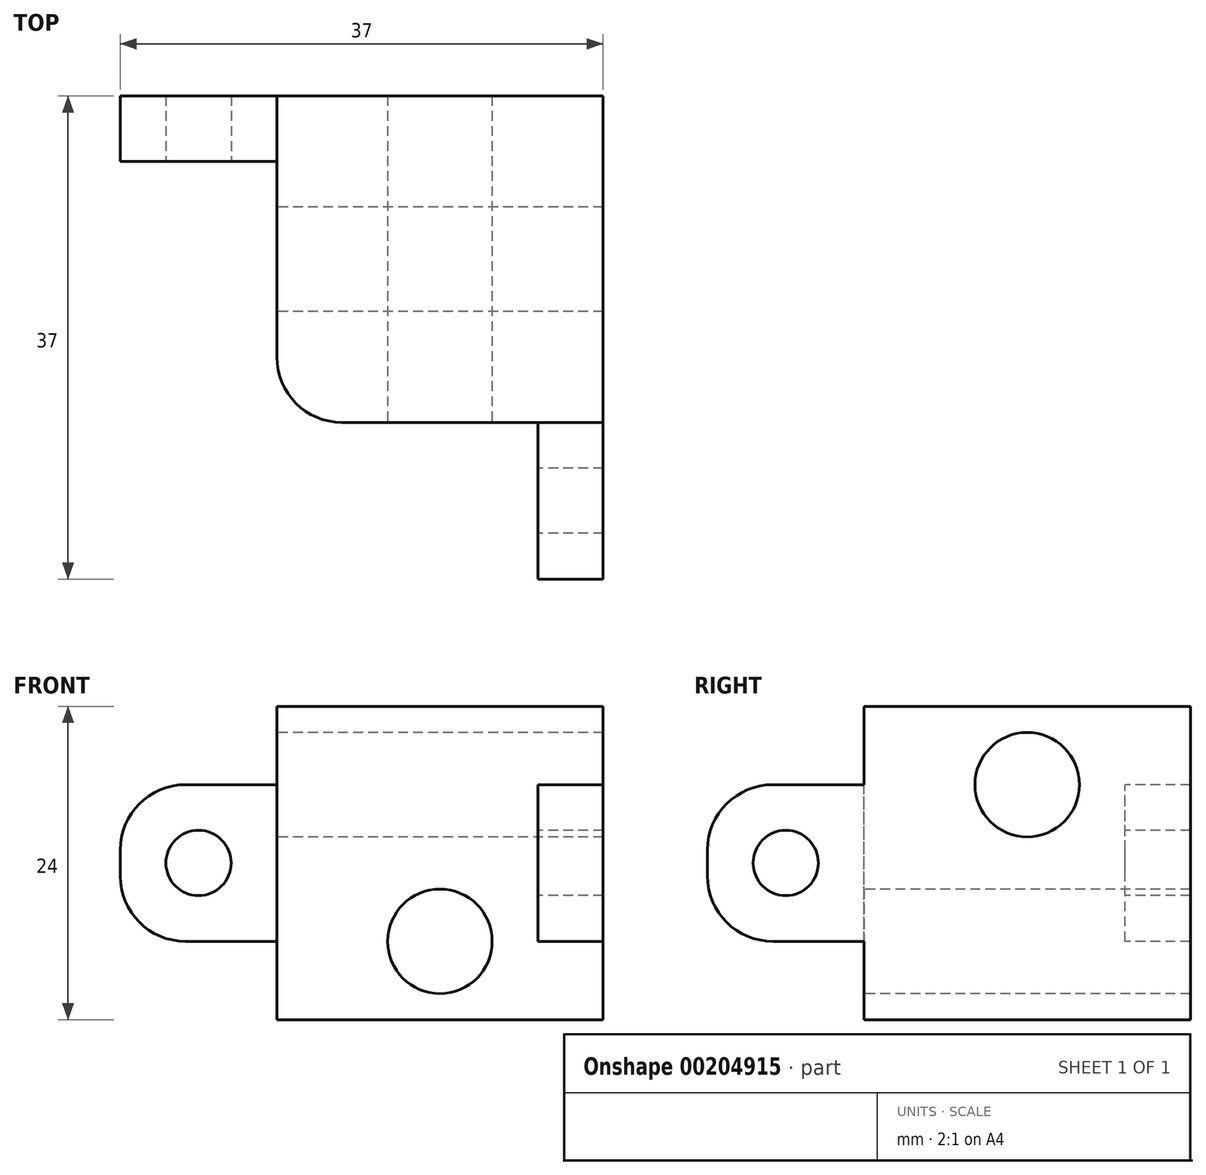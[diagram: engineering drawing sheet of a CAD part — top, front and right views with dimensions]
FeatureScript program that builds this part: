
annotation { "Feature Type Name" : "Feature", "Feature Type Description" : "" }
export const myFeature = defineFeature(function(context is Context, id is Id, definition is map)
    precondition{}
    {
        {
            var Q0;
            Q0=qCreatedBy(makeId("Front.planeOp"),FACE);
            var sketch = newSketch(context, id + "F0", { "sketchPlane" : qUnion([Q0])});
            skLineSegment(sketch, "E0.bottom", {"start": v(0, 0) * mm, "end": v(25, 0) * mm});
            skLineSegment(sketch, "E0.top", {"start": v(0, 45) * mm, "end": v(25, 45) * mm});
            skLineSegment(sketch, "E0.left", {"start": v(0, 0) * mm, "end": v(0, 45) * mm});
            skLineSegment(sketch, "E0.right", {"start": v(25, 0) * mm, "end": v(25, 45) * mm});
            skSolve(sketch);
        }
        {
            var Q0;
            Q0=makeQuery(id+"F0.imprint","IMPRINT",FACE,{"disambiguationData":[TD([[makeQuery(id+"F0.imprint","IMPRINT",EDGE,{"derivedFrom":sQuery(id+"F0.wireOp",EDGE,"E0.bottom")}),1.0]])]});
            extrude(context, id + "F1", {"entities" : qUnion([Q0]), "depth" : 25 * mm});
        }
        {
            var Q0;
            Q0=makeQuery(id+"F1.opExtrude","CAP_FACE",FACE,{"disambiguationData":[OSD([sQuery(id+"F0.wireOp",EDGE,"E0.bottom"),sQuery(id+"F0.wireOp",EDGE,"E0.top"),sQuery(id+"F0.wireOp",EDGE,"E0.left"),sQuery(id+"F0.wireOp",EDGE,"E0.right")])],"isStart":false});
            var sketch = newSketch(context, id + "F2", { "sketchPlane" : qUnion([Q0])});
            skLineSegment(sketch, "E1", {"start": v(12.5, 0) * mm, "end": v(12.5, 25) * mm});
            skCircle(sketch, "E2", {"center": v(12.5, 25) * mm, "radius": 4 * mm});
            skSolve(sketch);
        }
        {
            var Q0;
            Q0=makeQuery(id+"F2.imprint","IMPRINT",FACE,{"disambiguationData":[TD([[makeQuery(id+"F2.imprint","IMPRINT",EDGE,{"derivedFrom":sQuery(id+"F2.wireOp",EDGE,"E2")}),1.0]])]});
            extrude(context, id + "F3", {"entities" : qUnion([Q0]), "operationType" : NewBodyOperationType.REMOVE, "oppositeDirection" : true, "depth" : 25 * mm});
        }
        {
            var Q0;
            Q0=makeQuery(id+"F1.opExtrude","SWEPT_FACE",FACE,{"disambiguationData":[OSD([sQuery(id+"F0.wireOp",EDGE,"E0.left")])]});
            var sketch = newSketch(context, id + "F4", { "sketchPlane" : qUnion([Q0])});
            skLineSegment(sketch, "E3", {"start": v(12.5, 0) * mm, "end": v(12.5, 37) * mm});
            skCircle(sketch, "E4", {"center": v(12.5, 37) * mm, "radius": 4 * mm});
            skSolve(sketch);
        }
        {
            var Q0;
            Q0=makeQuery(id+"F4.imprint","IMPRINT",FACE,{"disambiguationData":[TD([[makeQuery(id+"F4.imprint","IMPRINT",EDGE,{"derivedFrom":sQuery(id+"F4.wireOp",EDGE,"E4")}),1.0]])]});
            extrude(context, id + "F5", {"entities" : qUnion([Q0]), "operationType" : NewBodyOperationType.REMOVE, "oppositeDirection" : true, "depth" : 25 * mm});
        }
        {
            var Q0;
            Q0=makeQuery(id+"F1.opExtrude","SWEPT_FACE",FACE,{"disambiguationData":[OSD([sQuery(id+"F0.wireOp",EDGE,"E0.left")])]});
            var sketch = newSketch(context, id + "F6", { "sketchPlane" : qUnion([Q0])});
            skLineSegment(sketch, "E5.bottom", {"start": v(0, 25) * mm, "end": v(5, 25) * mm});
            skLineSegment(sketch, "E5.top", {"start": v(0, 37) * mm, "end": v(5, 37) * mm});
            skLineSegment(sketch, "E5.left", {"start": v(0, 25) * mm, "end": v(0, 37) * mm});
            skLineSegment(sketch, "E5.right", {"start": v(5, 25) * mm, "end": v(5, 37) * mm});
            skSolve(sketch);
        }
        {
            var Q0;
            Q0=makeQuery(id+"F6.imprint","IMPRINT",FACE,{"disambiguationData":[TD([[makeQuery(id+"F6.imprint","IMPRINT",EDGE,{"derivedFrom":sQuery(id+"F6.wireOp",EDGE,"E5.bottom")}),1.0]])]});
            extrude(context, id + "F7", {"entities" : qUnion([Q0]), "operationType" : NewBodyOperationType.ADD, "depth" : 12 * mm});
        }
        {
            var Q0;
            Q0=makeQuery(id+"F7.opExtrude","SWEPT_FACE",FACE,{"disambiguationData":[OSD([sQuery(id+"F6.wireOp",EDGE,"E5.right")])]});
            var sketch = newSketch(context, id + "F8", { "sketchPlane" : qUnion([Q0])});
            skLineSegment(sketch, "E6", {"start": v(-6, 25) * mm, "end": v(-6, 37) * mm});
            skCircle(sketch, "E7", {"center": v(-6, 31) * mm, "radius": 2.5 * mm});
            skSolve(sketch);
        }
        {
            var Q0;
            {var subQ0=sQuery(id+"F8.wireOp",EDGE,"E7");var subQ1=sQuery(id+"F8.wireOp",EDGE,"E6");var subQ2=makeQuery(id+"F8.imprint","INTERSECT",VERTEX,{"disambiguationData":[OD(0.0)],"derivedFrom":[subQ1,subQ0]});Q0=makeQuery(id+"F8.imprint","IMPRINT",FACE,{"disambiguationData":[TD([[makeQuery(id+"F8.imprint","IMPRINT",EDGE,{"disambiguationData":[TD([[subQ2,-1.0]])],"derivedFrom":subQ1}),1.0]])]});}
            var Q1;
            {var subQ0=sQuery(id+"F8.wireOp",EDGE,"E7");var subQ1=sQuery(id+"F8.wireOp",EDGE,"E6");var subQ2=makeQuery(id+"F8.imprint","INTERSECT",VERTEX,{"disambiguationData":[OD(0.0)],"derivedFrom":[subQ1,subQ0]});Q1=makeQuery(id+"F8.imprint","IMPRINT",FACE,{"disambiguationData":[TD([[makeQuery(id+"F8.imprint","IMPRINT",EDGE,{"disambiguationData":[TD([[subQ2,-1.0]])],"derivedFrom":subQ1}),-1.0]])]});}
            extrude(context, id + "F9", {"entities" : qUnion([Q0, Q1]), "operationType" : NewBodyOperationType.REMOVE, "oppositeDirection" : true, "depth" : 25 * mm});
        }
        {
            var Q0;
            Q0=makeQuery(id+"F7.opExtrude","CAP_EDGE",EDGE,{"disambiguationData":[OSD([sQuery(id+"F6.wireOp",EDGE,"E5.top")])],"isStart":false});
            var Q1;
            Q1=makeQuery(id+"F7.opExtrude","CAP_EDGE",EDGE,{"disambiguationData":[OSD([sQuery(id+"F6.wireOp",EDGE,"E5.bottom")])],"isStart":false});
            var Q2;
            Q2=makeQuery(id+"F7.opExtrude","CAP_EDGE",EDGE,{"disambiguationData":[OSD([sQuery(id+"F6.wireOp",EDGE,"E5.top")])],"isStart":true});
            fillet(context, id + "F10", {"entities" : qUnion([Q0, Q1, Q2]), "radius" : 5 * mm, "tangentPropagation" : true, "allowEdgeOverflow" : false});
        }
        {
            var Q0;
            Q0=makeQuery(id+"F1.opExtrude","CAP_FACE",FACE,{"disambiguationData":[OSD([sQuery(id+"F0.wireOp",EDGE,"E0.bottom"),sQuery(id+"F0.wireOp",EDGE,"E0.top"),sQuery(id+"F0.wireOp",EDGE,"E0.left"),sQuery(id+"F0.wireOp",EDGE,"E0.right")])],"isStart":false});
            var sketch = newSketch(context, id + "F11", { "sketchPlane" : qUnion([Q0])});
            skLineSegment(sketch, "E8.bottom", {"start": v(25, 25) * mm, "end": v(20, 25) * mm});
            skLineSegment(sketch, "E8.top", {"start": v(25, 37) * mm, "end": v(20, 37) * mm});
            skLineSegment(sketch, "E8.left", {"start": v(25, 25) * mm, "end": v(25, 37) * mm});
            skLineSegment(sketch, "E8.right", {"start": v(20, 25) * mm, "end": v(20, 37) * mm});
            skSolve(sketch);
        }
        {
            var Q0;
            Q0=makeQuery(id+"F11.imprint","IMPRINT",FACE,{"disambiguationData":[TD([[makeQuery(id+"F11.imprint","IMPRINT",EDGE,{"derivedFrom":sQuery(id+"F11.wireOp",EDGE,"E8.bottom")}),-1.0]])]});
            extrude(context, id + "F12", {"entities" : qUnion([Q0]), "operationType" : NewBodyOperationType.ADD, "depth" : 12 * mm});
        }
        {
            var Q0;
            Q0=makeQuery(id+"F12.opExtrude","SWEPT_FACE",FACE,{"disambiguationData":[OSD([sQuery(id+"F11.wireOp",EDGE,"E8.right")])]});
            var sketch = newSketch(context, id + "F13", { "sketchPlane" : qUnion([Q0])});
            skLineSegment(sketch, "E9", {"start": v(31, 25) * mm, "end": v(31, 37) * mm});
            skCircle(sketch, "E10", {"center": v(31, 31) * mm, "radius": 2.5 * mm});
            skSolve(sketch);
        }
        {
            var Q0;
            {var subQ0=sQuery(id+"F13.wireOp",EDGE,"E10");var subQ1=sQuery(id+"F13.wireOp",EDGE,"E9");var subQ2=makeQuery(id+"F13.imprint","INTERSECT",VERTEX,{"disambiguationData":[OD(0.0)],"derivedFrom":[subQ1,subQ0]});Q0=makeQuery(id+"F13.imprint","IMPRINT",FACE,{"disambiguationData":[TD([[makeQuery(id+"F13.imprint","IMPRINT",EDGE,{"disambiguationData":[TD([[subQ2,-1.0]])],"derivedFrom":subQ1}),1.0]])]});}
            var Q1;
            {var subQ0=sQuery(id+"F13.wireOp",EDGE,"E10");var subQ1=sQuery(id+"F13.wireOp",EDGE,"E9");var subQ2=makeQuery(id+"F13.imprint","INTERSECT",VERTEX,{"disambiguationData":[OD(0.0)],"derivedFrom":[subQ1,subQ0]});Q1=makeQuery(id+"F13.imprint","IMPRINT",FACE,{"disambiguationData":[TD([[makeQuery(id+"F13.imprint","IMPRINT",EDGE,{"disambiguationData":[TD([[subQ2,-1.0]])],"derivedFrom":subQ1}),-1.0]])]});}
            extrude(context, id + "F14", {"entities" : qUnion([Q0, Q1]), "operationType" : NewBodyOperationType.REMOVE, "oppositeDirection" : true, "depth" : 25 * mm});
        }
        {
            var Q0;
            Q0=makeQuery(id+"F12.opExtrude","CAP_EDGE",EDGE,{"disambiguationData":[OSD([sQuery(id+"F11.wireOp",EDGE,"E8.top")])],"isStart":false});
            var Q1;
            Q1=makeQuery(id+"F12.opExtrude","CAP_EDGE",EDGE,{"disambiguationData":[OSD([sQuery(id+"F11.wireOp",EDGE,"E8.bottom")])],"isStart":false});
            var Q2;
            Q2=makeQuery(id+"F12.opExtrude","CAP_EDGE",EDGE,{"disambiguationData":[OSD([sQuery(id+"F11.wireOp",EDGE,"E8.bottom")])],"isStart":true});
            fillet(context, id + "F15", {"entities" : qUnion([Q0, Q1, Q2]), "radius" : 5 * mm, "tangentPropagation" : true, "allowEdgeOverflow" : false});
        }
        {
            var Q0;
            Q0=makeQuery(id+"F1.opExtrude","SWEPT_FACE",FACE,{"disambiguationData":[OSD([sQuery(id+"F0.wireOp",EDGE,"E0.left")])]});
            var sketch = newSketch(context, id + "F16", { "sketchPlane" : qUnion([Q0])});
            skLineSegment(sketch, "E11.bottom", {"start": v(25, 4) * mm, "end": v(6, 4) * mm});
            skLineSegment(sketch, "E11.top", {"start": v(25, 10) * mm, "end": v(6, 10) * mm});
            skLineSegment(sketch, "E11.left", {"start": v(25, 4) * mm, "end": v(25, 10) * mm});
            skLineSegment(sketch, "E11.right", {"start": v(6, 4) * mm, "end": v(6, 10) * mm});
            skSolve(sketch);
        }
        {
            var Q0;
            Q0=makeQuery(id+"F16.imprint","IMPRINT",FACE,{"disambiguationData":[TD([[makeQuery(id+"F16.imprint","IMPRINT",EDGE,{"derivedFrom":sQuery(id+"F16.wireOp",EDGE,"E11.bottom")}),-1.0]])]});
            extrude(context, id + "F17", {"entities" : qUnion([Q0]), "operationType" : NewBodyOperationType.REMOVE, "oppositeDirection" : true, "depth" : 19 * mm});
        }
        {
            var Q0;
            Q0=makeQuery(id+"F1.opExtrude","SWEPT_FACE",FACE,{"disambiguationData":[OSD([sQuery(id+"F0.wireOp",EDGE,"E0.bottom")])]});
            var sketch = newSketch(context, id + "F18", { "sketchPlane" : qUnion([Q0])});
            skLineSegment(sketch, "E12", {"start": v(0, 25) * mm, "end": v(7.78, 17.22) * mm});
            skCircle(sketch, "E13.cCircle", {"center": v(7.78, 17.22) * mm, "radius": 2.5 * mm, "construction": true});
            skLineSegment(sketch, "E13.0", {"start": v(5.28, 15.78) * mm, "end": v(5.28, 18.67) * mm});
            skLineSegment(sketch, "E13.1", {"start": v(5.28, 18.67) * mm, "end": v(7.78, 20.1) * mm});
            skLineSegment(sketch, "E13.2", {"start": v(7.78, 20.1) * mm, "end": v(10.28, 18.67) * mm});
            skLineSegment(sketch, "E13.3", {"start": v(10.28, 18.67) * mm, "end": v(10.28, 15.78) * mm});
            skLineSegment(sketch, "E13.4", {"start": v(10.28, 15.78) * mm, "end": v(7.78, 14.34) * mm});
            skLineSegment(sketch, "E13.5", {"start": v(7.78, 14.34) * mm, "end": v(5.28, 15.78) * mm});
            skPoint(sketch, "E13.0.midPoint", {"position": v(5.28, 17.22) * mm});
            skSolve(sketch);
        }
        {
            var Q0;
            {var subQ3=sQuery(id+"F18.wireOp",EDGE,"E13.0");Q0=makeQuery(id+"F18.imprint","IMPRINT",FACE,{"disambiguationData":[TD([[makeQuery(id+"F18.imprint","IMPRINT",EDGE,{"derivedFrom":subQ3}),-1.0]])]});}
            extrude(context, id + "F19", {"entities" : qUnion([Q0]), "operationType" : NewBodyOperationType.REMOVE, "oppositeDirection" : true, "depth" : 12 * mm});
        }
        {
            var Q0;
            Q0=makeQuery(id+"F17.boolean.opBoolean","COPY",EDGE,{"derivedFrom":makeQuery(id+"F17.opExtrude","CAP_EDGE",EDGE,{"disambiguationData":[OSD([sQuery(id+"F16.wireOp",EDGE,"E11.right")])],"isStart":false})});
            fillet(context, id + "F20", {"entities" : qUnion([Q0]), "radius" : 5 * mm, "tangentPropagation" : true, "allowEdgeOverflow" : false});
        }
        {
            var Q0;
            {var subQ0=sQuery(id+"F0.wireOp",EDGE,"E0.bottom");var subQ1=sQuery(id+"F0.wireOp",EDGE,"E0.left");Q0=makeQuery(id+"F17.boolean.opBoolean","SPLIT",EDGE,{"disambiguationData":[TD([makeQuery(id+"F1.opExtrude","SWEPT_FACE",FACE,{"disambiguationData":[OSD([subQ0])]})])],"derivedFrom":makeQuery(id+"F1.opExtrude","CAP_EDGE",EDGE,{"disambiguationData":[OSD([subQ1])],"isStart":false})});}
            var Q1;
            {var subQ0=sQuery(id+"F0.wireOp",EDGE,"E0.left");var subQ1=sQuery(id+"F0.wireOp",EDGE,"E0.top");Q1=makeQuery(id+"F17.boolean.opBoolean","SPLIT",EDGE,{"disambiguationData":[TD([makeQuery(id+"F1.opExtrude","SWEPT_FACE",FACE,{"disambiguationData":[OSD([subQ1])]})])],"derivedFrom":makeQuery(id+"F1.opExtrude","CAP_EDGE",EDGE,{"disambiguationData":[OSD([subQ0])],"isStart":false})});}
            fillet(context, id + "F21", {"entities" : qUnion([Q0, Q1]), "radius" : 5 * mm, "tangentPropagation" : true, "allowEdgeOverflow" : false});
        }
        {
            var Q0;
            Q0=makeQuery(id+"F1.opExtrude","SWEPT_FACE",FACE,{"disambiguationData":[OSD([sQuery(id+"F0.wireOp",EDGE,"E0.top")])]});
            extrude(context, id + "F22", {"entities" : qUnion([Q0]), "operationType" : NewBodyOperationType.REMOVE, "oppositeDirection" : true, "depth" : 2 * mm});
        }
        {
            var Q0;
            Q0=makeQuery(id+"F1.opExtrude","SWEPT_FACE",FACE,{"disambiguationData":[OSD([sQuery(id+"F0.wireOp",EDGE,"E0.bottom")])]});
            extrude(context, id + "F23", {"entities" : qUnion([Q0]), "operationType" : NewBodyOperationType.REMOVE, "oppositeDirection" : true, "depth" : 19 * mm});
        }
        {
            var Q0;
            Q0=makeQuery(id+"F19.boolean.opBoolean","COPY",FACE,{"derivedFrom":makeQuery(id+"F19.opExtrude","CAP_FACE",FACE,{"disambiguationData":[OSD([sQuery(id+"F18.wireOp",EDGE,"E13.0"),sQuery(id+"F18.wireOp",EDGE,"E13.1"),sQuery(id+"F18.wireOp",EDGE,"E13.2"),sQuery(id+"F18.wireOp",EDGE,"E13.3"),sQuery(id+"F18.wireOp",EDGE,"E13.4"),sQuery(id+"F18.wireOp",EDGE,"E13.5")])],"isStart":false})});
            var Q1;
            Q1=makeQuery(id+"F23.boolean.opBoolean","COPY",FACE,{"derivedFrom":makeQuery(id+"F23.opExtrude","CAP_FACE",FACE,{"disambiguationData":[OSD([sQuery(id+"F0.wireOp",EDGE,"E0.bottom")])],"isStart":false})});
            extrude(context, id + "F24", {"entities" : qUnion([Q0]), "operationType" : NewBodyOperationType.REMOVE, "endBound" : BoundingType.UP_TO_SURFACE, "oppositeDirection" : true, "endBoundEntityFace" : qUnion([Q1]), "depth" : 25 * mm});
        }
    });
